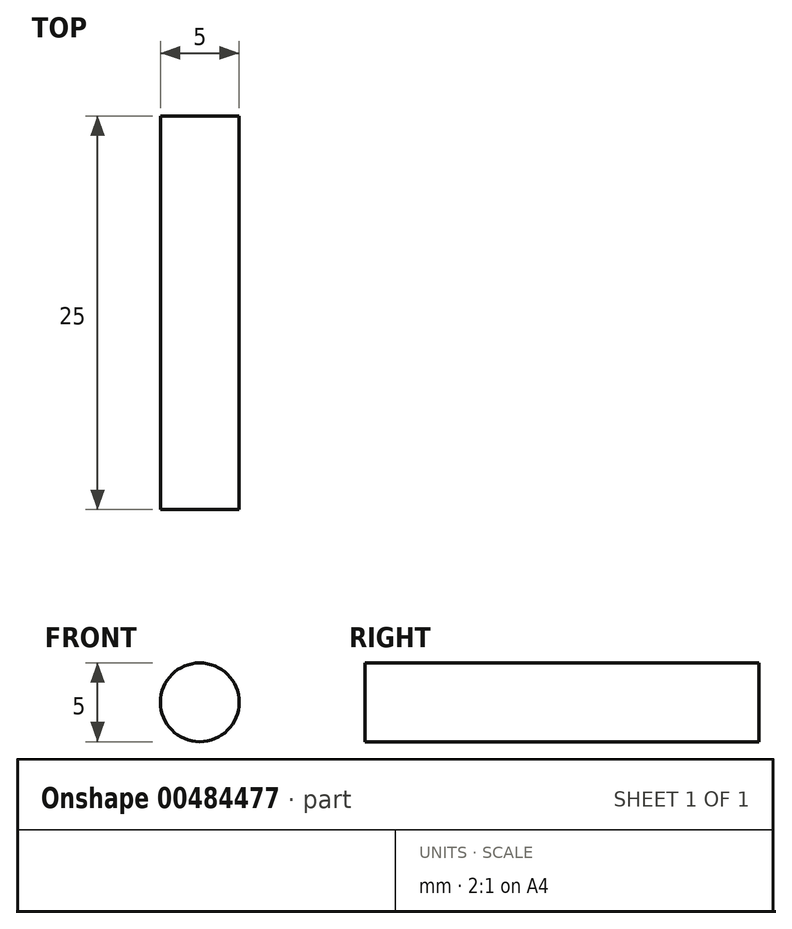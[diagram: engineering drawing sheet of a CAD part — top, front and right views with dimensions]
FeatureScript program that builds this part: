
annotation { "Feature Type Name" : "Feature", "Feature Type Description" : "" }
export const myFeature = defineFeature(function(context is Context, id is Id, definition is map)
    precondition{}
    {
        {
            var Q0;
            Q0=qCreatedBy(makeId("Front.planeOp"),FACE);
            var sketch = newSketch(context, id + "F0", { "sketchPlane" : qUnion([Q0])});
            skCircle(sketch, "E0", {"center": v(0, 0) * mm, "radius": 2.5 * mm});
            skSolve(sketch);
        }
        {
            var Q0;
            Q0 = qSketchRegion(id + "F0", true);
            extrude(context, id + "F1", {"entities" : qUnion([Q0]), "depth" : 25 * mm});
        }
    });
